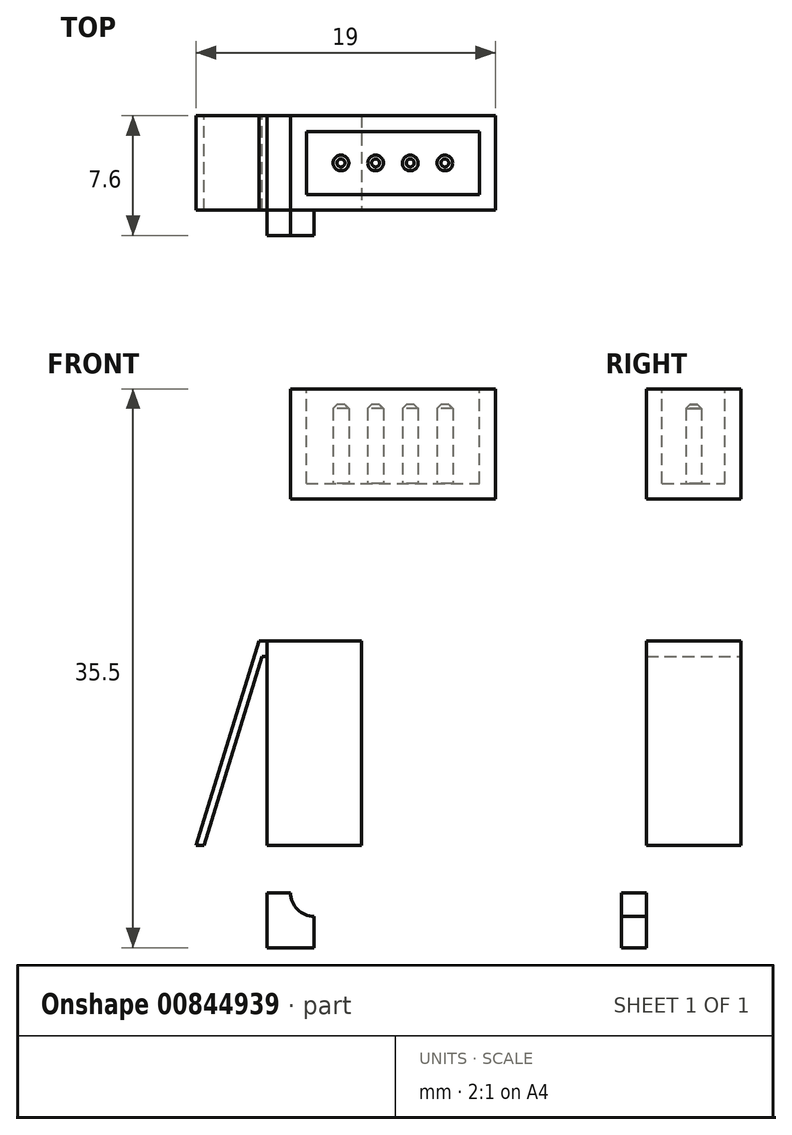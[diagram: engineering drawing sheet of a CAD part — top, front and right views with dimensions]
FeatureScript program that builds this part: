
annotation { "Feature Type Name" : "Feature", "Feature Type Description" : "" }
export const myFeature = defineFeature(function(context is Context, id is Id, definition is map)
    precondition{}
    {
        {
            var Q0;
            Q0=qCreatedBy(makeId("Front.planeOp"),FACE);
            var sketch = newSketch(context, id + "F0", { "sketchPlane" : qUnion([Q0])});
            skLineSegment(sketch, "E0.bottom", {"start": v(0, 0) * mm, "end": v(16, 0) * mm});
            skLineSegment(sketch, "E0.top", {"start": v(0, 39.5) * mm, "end": v(16, 39.5) * mm});
            skLineSegment(sketch, "E0.left", {"start": v(0, 0) * mm, "end": v(0, 39.5) * mm});
            skLineSegment(sketch, "E0.right", {"start": v(16, 0) * mm, "end": v(16, 39.5) * mm});
            skLineSegment(sketch, "E1.bottom", {"start": v(0, 0) * mm, "end": v(3, 0) * mm});
            skLineSegment(sketch, "E1.top", {"start": v(0, 3.5) * mm, "end": v(3, 3.5) * mm});
            skLineSegment(sketch, "E1.left", {"start": v(0, 0) * mm, "end": v(0, 3.5) * mm});
            skLineSegment(sketch, "E1.right", {"start": v(3, 0) * mm, "end": v(3, 3.5) * mm});
            skLineSegment(sketch, "E2", {"start": v(3, 3.5) * mm, "end": v(3, 22.5) * mm});
            skCircle(sketch, "E3", {"center": v(3, 22.5) * mm, "radius": 1.5 * mm});
            skCircle(sketch, "E4", {"center": v(3, 3.5) * mm, "radius": 1.5 * mm});
            skLineSegment(sketch, "E5.bottom", {"start": v(16, 39.5) * mm, "end": v(13.5, 39.5) * mm});
            skLineSegment(sketch, "E5.top", {"start": v(16, 37) * mm, "end": v(13.5, 37) * mm});
            skLineSegment(sketch, "E5.left", {"start": v(16, 39.5) * mm, "end": v(16, 37) * mm});
            skLineSegment(sketch, "E5.right", {"start": v(13.5, 39.5) * mm, "end": v(13.5, 37) * mm});
            skCircle(sketch, "E6", {"center": v(13.5, 37) * mm, "radius": 1.5 * mm});
            skLineSegment(sketch, "E7.bottom", {"start": v(0, 39.5) * mm, "end": v(2.5, 39.5) * mm});
            skLineSegment(sketch, "E7.top", {"start": v(0, 37) * mm, "end": v(2.5, 37) * mm});
            skLineSegment(sketch, "E7.left", {"start": v(0, 39.5) * mm, "end": v(0, 37) * mm});
            skLineSegment(sketch, "E7.right", {"start": v(2.5, 39.5) * mm, "end": v(2.5, 37) * mm});
            skCircle(sketch, "E8", {"center": v(2.5, 37) * mm, "radius": 1.5 * mm});
            skSolve(sketch);
        }
        {
            var Q0;
            {var subQ7=sQuery(id+"F0.wireOp",EDGE,"E0.bottom");Q0=makeQuery(id+"F0.imprint","IMPRINT",FACE,{"disambiguationData":[TD([[makeQuery(id+"F0.imprint","IMPRINT",EDGE,{"derivedFrom":subQ7}),1.0]])]});}
            var Q1;
            {var subQ1=sQuery(id+"F0.wireOp",EDGE,"E1.bottom");Q1=makeQuery(id+"F0.imprint","IMPRINT",FACE,{"disambiguationData":[TD([[makeQuery(id+"F0.imprint","IMPRINT",EDGE,{"derivedFrom":subQ1}),1.0]])]});}
            var Q2;
            {var subQ1=sQuery(id+"F0.wireOp",EDGE,"E7.bottom");Q2=makeQuery(id+"F0.imprint","IMPRINT",FACE,{"disambiguationData":[TD([[makeQuery(id+"F0.imprint","IMPRINT",EDGE,{"derivedFrom":subQ1}),-1.0]])]});}
            var Q3;
            {var subQ1=sQuery(id+"F0.wireOp",EDGE,"E5.bottom");Q3=makeQuery(id+"F0.imprint","IMPRINT",FACE,{"disambiguationData":[TD([[makeQuery(id+"F0.imprint","IMPRINT",EDGE,{"derivedFrom":subQ1}),1.0]])]});}
            extrude(context, id + "F1", {"entities" : qUnion([Q0, Q1, Q2, Q3]), "depth" : 1.6 * mm, "offsetDistance" : 25 * mm});
        }
        {
            var Q0;
            Q0=makeQuery(id+"F1.opExtrude","CAP_FACE",FACE,{"disambiguationData":[OSD([sQuery(id+"F0.wireOp",EDGE,"E0.bottom"),sQuery(id+"F0.wireOp",EDGE,"E0.top"),sQuery(id+"F0.wireOp",EDGE,"E0.left"),sQuery(id+"F0.wireOp",EDGE,"E0.right"),sQuery(id+"F0.wireOp",EDGE,"E1.bottom"),sQuery(id+"F0.wireOp",EDGE,"E1.left"),sQuery(id+"F0.wireOp",EDGE,"E3"),sQuery(id+"F0.wireOp",EDGE,"E4")])],"isStart":true});
            var sketch = newSketch(context, id + "F2", { "sketchPlane" : qUnion([Q0])});
            skLineSegment(sketch, "E9", {"start": v(-3, 22.5) * mm, "end": v(-3, 3.5) * mm});
            skLineSegment(sketch, "E10", {"start": v(-3, 13) * mm, "end": v(-3, 6.5) * mm});
            skLineSegment(sketch, "E11.bottom", {"start": v(0, 6.5) * mm, "end": v(-6, 6.5) * mm});
            skLineSegment(sketch, "E11.top", {"start": v(0, 19.5) * mm, "end": v(-6, 19.5) * mm});
            skLineSegment(sketch, "E11.left", {"start": v(0, 6.5) * mm, "end": v(0, 19.5) * mm});
            skLineSegment(sketch, "E11.right", {"start": v(-6, 6.5) * mm, "end": v(-6, 19.5) * mm});
            skSolve(sketch);
        }
        {
            var Q0;
            {var subQ3=sQuery(id+"F2.wireOp",EDGE,"E11.left");Q0=makeQuery(id+"F2.imprint","IMPRINT",FACE,{"disambiguationData":[TD([[makeQuery(id+"F2.imprint","IMPRINT",EDGE,{"derivedFrom":subQ3}),1.0]])]});}
            var Q1;
            {var subQ3=sQuery(id+"F2.wireOp",EDGE,"E11.right");Q1=makeQuery(id+"F2.imprint","IMPRINT",FACE,{"disambiguationData":[TD([[makeQuery(id+"F2.imprint","IMPRINT",EDGE,{"derivedFrom":subQ3}),-1.0]])]});}
            extrude(context, id + "F3", {"entities" : qUnion([Q0, Q1]), "depth" : 6 * mm, "offsetDistance" : 25 * mm});
        }
        {
            var Q0;
            Q0=makeQuery(id+"F1.opExtrude","CAP_FACE",FACE,{"disambiguationData":[OSD([sQuery(id+"F0.wireOp",EDGE,"E0.bottom"),sQuery(id+"F0.wireOp",EDGE,"E0.top"),sQuery(id+"F0.wireOp",EDGE,"E0.left"),sQuery(id+"F0.wireOp",EDGE,"E0.right"),sQuery(id+"F0.wireOp",EDGE,"E1.bottom"),sQuery(id+"F0.wireOp",EDGE,"E1.left"),sQuery(id+"F0.wireOp",EDGE,"E3"),sQuery(id+"F0.wireOp",EDGE,"E4")])],"isStart":true});
            var sketch = newSketch(context, id + "F4", { "sketchPlane" : qUnion([Q0])});
            skLineSegment(sketch, "E12.bottom", {"start": v(0, 39.5) * mm, "end": v(-1.5, 39.5) * mm});
            skLineSegment(sketch, "E12.top", {"start": v(0, 35.5) * mm, "end": v(-1.5, 35.5) * mm});
            skLineSegment(sketch, "E12.left", {"start": v(0, 39.5) * mm, "end": v(0, 35.5) * mm});
            skLineSegment(sketch, "E12.right", {"start": v(-1.5, 39.5) * mm, "end": v(-1.5, 35.5) * mm});
            skLineSegment(sketch, "E13.bottom", {"start": v(-1.5, 35.5) * mm, "end": v(-14.5, 35.5) * mm});
            skLineSegment(sketch, "E13.top", {"start": v(-1.5, 28.5) * mm, "end": v(-14.5, 28.5) * mm});
            skLineSegment(sketch, "E13.left", {"start": v(-1.5, 35.5) * mm, "end": v(-1.5, 28.5) * mm});
            skLineSegment(sketch, "E13.right", {"start": v(-14.5, 35.5) * mm, "end": v(-14.5, 28.5) * mm});
            skSolve(sketch);
        }
        {
            var Q0;
            Q0=makeQuery(id+"F4.imprint","IMPRINT",FACE,{"disambiguationData":[TD([[makeQuery(id+"F4.imprint","IMPRINT",EDGE,{"derivedFrom":sQuery(id+"F4.wireOp",EDGE,"E13.bottom")}),1.0]])]});
            extrude(context, id + "F5", {"entities" : qUnion([Q0]), "depth" : 6 * mm, "offsetDistance" : 25 * mm});
        }
        {
            var Q0;
            Q0=makeQuery(id+"F3.opExtrude","CAP_FACE",FACE,{"disambiguationData":[OSD([sQuery(id+"F2.wireOp",EDGE,"E11.bottom"),sQuery(id+"F2.wireOp",EDGE,"E11.top"),sQuery(id+"F2.wireOp",EDGE,"E11.left"),sQuery(id+"F2.wireOp",EDGE,"E11.right")])],"isStart":false});
            var sketch = newSketch(context, id + "F6", { "sketchPlane" : qUnion([Q0])});
            skLineSegment(sketch, "E14", {"start": v(0, 19.5) * mm, "end": v(0.5, 19.5) * mm});
            skLineSegment(sketch, "E15", {"start": v(0, 6.5) * mm, "end": v(4, 6.5) * mm});
            skLineSegment(sketch, "E16", {"start": v(4, 6.5) * mm, "end": v(4.5, 6.5) * mm});
            skLineSegment(sketch, "E17", {"start": v(0, 19.5) * mm, "end": v(4, 6.5) * mm});
            skLineSegment(sketch, "E18", {"start": v(0.5, 19.5) * mm, "end": v(4.5, 6.5) * mm});
            skLineSegment(sketch, "E19", {"start": v(0, 19.5) * mm, "end": v(0, 18.5) * mm});
            skLineSegment(sketch, "E20", {"start": v(0, 18.5) * mm, "end": v(0.3, 18.5) * mm});
            skSolve(sketch);
        }
        {
            var Q0;
            {var subQ3=sQuery(id+"F6.wireOp",EDGE,"E14");Q0=makeQuery(id+"F6.imprint","IMPRINT",FACE,{"disambiguationData":[TD([[makeQuery(id+"F6.imprint","IMPRINT",EDGE,{"derivedFrom":subQ3}),-1.0]])]});}
            var Q1;
            {var subQ0=sQuery(id+"F6.wireOp",EDGE,"E19");Q1=makeQuery(id+"F6.imprint","IMPRINT",FACE,{"disambiguationData":[TD([[makeQuery(id+"F6.imprint","IMPRINT",EDGE,{"derivedFrom":subQ0}),-1.0]])]});}
            extrude(context, id + "F7", {"entities" : qUnion([Q0, Q1]), "oppositeDirection" : true, "depth" : 6 * mm, "offsetDistance" : 25 * mm});
        }
        {
            var Q0;
            Q0=makeQuery(id+"F5.opExtrude","SWEPT_FACE",FACE,{"disambiguationData":[OSD([sQuery(id+"F4.wireOp",EDGE,"E13.bottom")])]});
            var sketch = newSketch(context, id + "F8", { "sketchPlane" : qUnion([Q0])});
            skLineSegment(sketch, "E21.bottom", {"start": v(1.5, 0) * mm, "end": v(2.5, 0) * mm});
            skLineSegment(sketch, "E21.top", {"start": v(1.5, 1) * mm, "end": v(2.5, 1) * mm});
            skLineSegment(sketch, "E21.left", {"start": v(1.5, 0) * mm, "end": v(1.5, 1) * mm});
            skLineSegment(sketch, "E21.right", {"start": v(2.5, 0) * mm, "end": v(2.5, 1) * mm});
            skLineSegment(sketch, "E22.bottom", {"start": v(2.5, 1) * mm, "end": v(13.5, 1) * mm});
            skLineSegment(sketch, "E22.top", {"start": v(2.5, 5) * mm, "end": v(13.5, 5) * mm});
            skLineSegment(sketch, "E22.left", {"start": v(2.5, 1) * mm, "end": v(2.5, 5) * mm});
            skLineSegment(sketch, "E22.right", {"start": v(13.5, 1) * mm, "end": v(13.5, 5) * mm});
            skSolve(sketch);
        }
        {
            var Q0;
            Q0=makeQuery(id+"F8.imprint","IMPRINT",FACE,{"disambiguationData":[TD([[makeQuery(id+"F8.imprint","IMPRINT",EDGE,{"derivedFrom":sQuery(id+"F8.wireOp",EDGE,"E22.bottom")}),1.0]])]});
            extrude(context, id + "F9", {"entities" : qUnion([Q0]), "operationType" : NewBodyOperationType.REMOVE, "oppositeDirection" : true, "depth" : 6 * mm, "offsetDistance" : 25 * mm});
        }
        {
            var Q0;
            Q0=makeQuery(id+"F9.boolean.opBoolean","COPY",FACE,{"derivedFrom":makeQuery(id+"F9.opExtrude","CAP_FACE",FACE,{"disambiguationData":[OSD([sQuery(id+"F8.wireOp",EDGE,"E22.bottom"),sQuery(id+"F8.wireOp",EDGE,"E22.top"),sQuery(id+"F8.wireOp",EDGE,"E22.left"),sQuery(id+"F8.wireOp",EDGE,"E22.right")])],"isStart":false})});
            var sketch = newSketch(context, id + "F10", { "sketchPlane" : qUnion([Q0])});
            skLineSegment(sketch, "E23", {"start": v(2.5, 3) * mm, "end": v(4.7, 3) * mm});
            skCircle(sketch, "E24", {"center": v(4.7, 3) * mm, "radius": 0.5 * mm});
            skCircle(sketch, "E25.1.0.0", {"center": v(6.9, 3) * mm, "radius": 0.5 * mm});
            skCircle(sketch, "E25.2.0.0", {"center": v(9.1, 3) * mm, "radius": 0.5 * mm});
            skCircle(sketch, "E25.3.0.0", {"center": v(11.3, 3) * mm, "radius": 0.5 * mm});
            skLineSegment(sketch, "E25.direction1", {"start": v(4.7, 3) * mm, "end": v(6.9, 3) * mm, "construction": true});
            skSolve(sketch);
        }
        {
            var Q0;
            Q0=makeQuery(id+"F10.imprint","IMPRINT",FACE,{"disambiguationData":[TD([[makeQuery(id+"F10.imprint","IMPRINT",EDGE,{"derivedFrom":sQuery(id+"F10.wireOp",EDGE,"E25.3.0.0")}),1.0]])]});
            var Q1;
            Q1=makeQuery(id+"F10.imprint","IMPRINT",FACE,{"disambiguationData":[TD([[makeQuery(id+"F10.imprint","IMPRINT",EDGE,{"derivedFrom":sQuery(id+"F10.wireOp",EDGE,"E25.2.0.0")}),1.0]])]});
            var Q2;
            Q2=makeQuery(id+"F10.imprint","IMPRINT",FACE,{"disambiguationData":[TD([[makeQuery(id+"F10.imprint","IMPRINT",EDGE,{"derivedFrom":sQuery(id+"F10.wireOp",EDGE,"E25.1.0.0")}),1.0]])]});
            var Q3;
            Q3=makeQuery(id+"F10.imprint","IMPRINT",FACE,{"disambiguationData":[TD([[makeQuery(id+"F10.imprint","IMPRINT",EDGE,{"derivedFrom":sQuery(id+"F10.wireOp",EDGE,"E24")}),1.0]])]});
            extrude(context, id + "F11", {"entities" : qUnion([Q0, Q1, Q2, Q3]), "operationType" : NewBodyOperationType.ADD, "depth" : 5 * mm, "offsetDistance" : 25 * mm});
        }
        {
            var Q0;
            Q0=makeQuery(id+"F11.opExtrude","CAP_EDGE",EDGE,{"disambiguationData":[OSD([sQuery(id+"F10.wireOp",EDGE,"E24")])],"isStart":false});
            var Q1;
            Q1=makeQuery(id+"F11.opExtrude","CAP_EDGE",EDGE,{"disambiguationData":[OSD([sQuery(id+"F10.wireOp",EDGE,"E25.1.0.0")])],"isStart":false});
            var Q2;
            Q2=makeQuery(id+"F11.opExtrude","CAP_EDGE",EDGE,{"disambiguationData":[OSD([sQuery(id+"F10.wireOp",EDGE,"E25.2.0.0")])],"isStart":false});
            var Q3;
            Q3=makeQuery(id+"F11.opExtrude","CAP_EDGE",EDGE,{"disambiguationData":[OSD([sQuery(id+"F10.wireOp",EDGE,"E25.3.0.0")])],"isStart":false});
            chamfer(context, id + "F12", {"entities" : qUnion([Q0, Q1, Q2, Q3]), "width" : .25 * mm, "tangentPropagation" : true});
        }
    });
